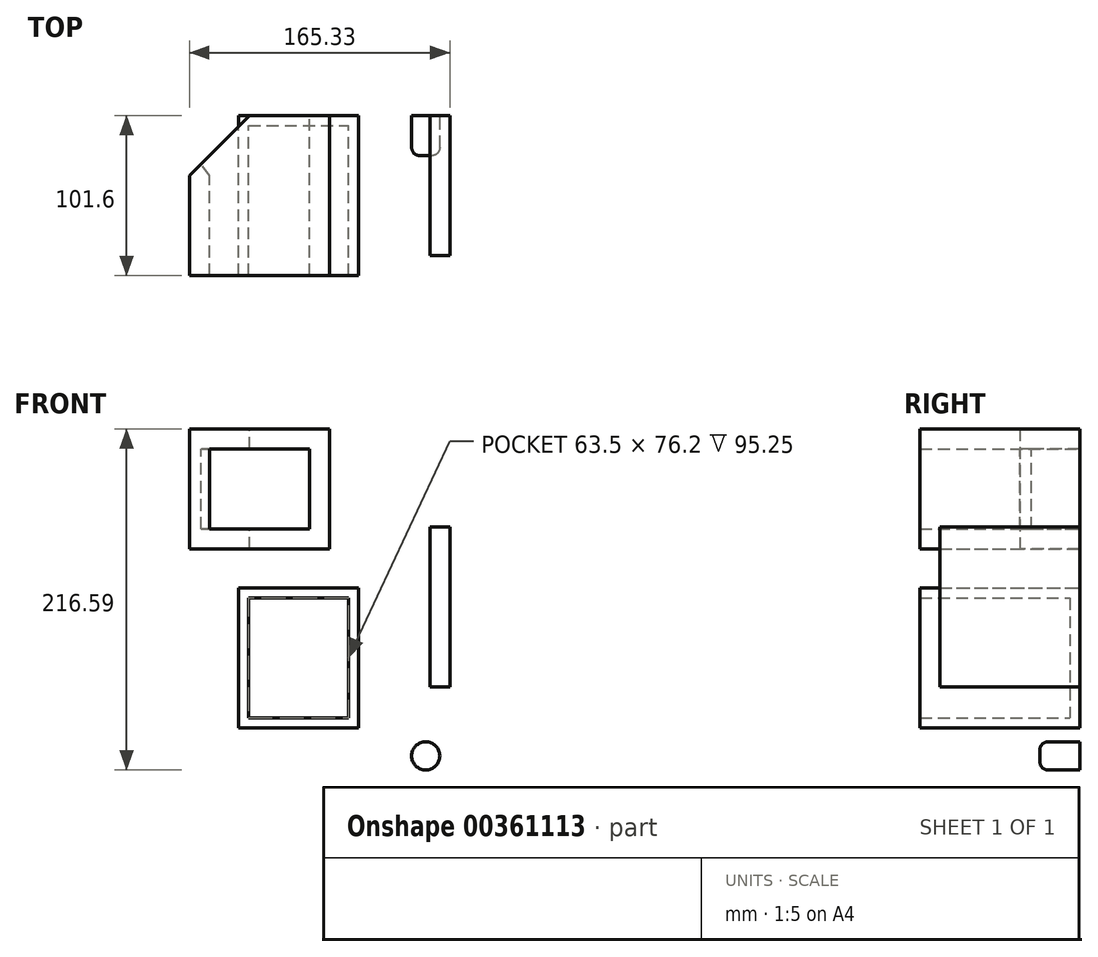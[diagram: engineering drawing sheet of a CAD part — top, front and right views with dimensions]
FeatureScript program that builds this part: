
annotation { "Feature Type Name" : "Feature", "Feature Type Description" : "" }
export const myFeature = defineFeature(function(context is Context, id is Id, definition is map)
    precondition{}
    {
        {
            var Q0;
            Q0=qCreatedBy(makeId("Front.planeOp"),FACE);
            var sketch = newSketch(context, id + "F0", { "sketchPlane" : qUnion([Q0])});
            skLineSegment(sketch, "E0.bottom", {"start": v(45.2, 26.89) * mm, "end": v(57.9, 26.89) * mm});
            skLineSegment(sketch, "E0.top", {"start": v(45.2, -74.71) * mm, "end": v(57.9, -74.71) * mm});
            skLineSegment(sketch, "E0.left", {"start": v(45.2, 26.89) * mm, "end": v(45.2, -74.71) * mm});
            skLineSegment(sketch, "E0.right", {"start": v(57.9, 26.89) * mm, "end": v(57.9, -74.71) * mm});
            skLineSegment(sketch, "E1.bottom", {"start": v(-31.24, 25.48) * mm, "end": v(-94.74, 25.48) * mm});
            skLineSegment(sketch, "E1.top", {"start": v(-31.24, 76.28) * mm, "end": v(-94.74, 76.28) * mm});
            skLineSegment(sketch, "E1.left", {"start": v(-31.24, 25.48) * mm, "end": v(-31.24, 76.28) * mm});
            skLineSegment(sketch, "E1.right", {"start": v(-94.74, 25.48) * mm, "end": v(-94.74, 76.28) * mm});
            skLineSegment(sketch, "E2.bottom", {"start": v(-107.44, 88.98) * mm, "end": v(-18.54, 88.98) * mm});
            skLineSegment(sketch, "E2.top", {"start": v(-107.44, 12.78) * mm, "end": v(-18.54, 12.78) * mm});
            skLineSegment(sketch, "E2.left", {"start": v(-107.44, 88.98) * mm, "end": v(-107.44, 12.78) * mm});
            skLineSegment(sketch, "E2.right", {"start": v(-18.54, 88.98) * mm, "end": v(-18.54, 12.78) * mm});
            skSolve(sketch);
        }
        {
            var Q0;
            Q0=makeQuery(id+"F0.imprint","IMPRINT",FACE,{"disambiguationData":[TD([[makeQuery(id+"F0.imprint","IMPRINT",EDGE,{"derivedFrom":sQuery(id+"F0.wireOp",EDGE,"E0.bottom")}),-1.0]])]});
            extrude(context, id + "F1", {"entities" : qUnion([Q0]), "depth" : 88.9 * mm});
        }
        {
            var Q0;
            Q0=makeQuery(id+"F0.imprint","IMPRINT",FACE,{"disambiguationData":[TD([[makeQuery(id+"F0.imprint","IMPRINT",EDGE,{"derivedFrom":sQuery(id+"F0.wireOp",EDGE,"E1.bottom")}),1.0]])]});
            extrude(context, id + "F2", {"entities" : qUnion([Q0]), "depth" : 101.6 * mm});
        }
        {
            var Q0;
            Q0=makeQuery(id+"F2.opExtrude","CAP_EDGE",EDGE,{"disambiguationData":[OSD([sQuery(id+"F0.wireOp",EDGE,"E2.left")])],"isStart":true});
            chamfer(context, id + "F3", {"entities" : qUnion([Q0]), "width" : 38.1 * mm, "tangentPropagation" : true});
        }
        {
            var Q0;
            Q0=makeQuery(id+"F3.opChamfer","BLEND_EDGE",EDGE,{"blendedFrom":[makeQuery(id+"F2.opExtrude","CAP_EDGE",EDGE,{"disambiguationData":[OSD([sQuery(id+"F0.wireOp",EDGE,"E2.left")])],"isStart":true}),makeQuery(id+"F2.opExtrude","SWEPT_FACE",FACE,{"disambiguationData":[OSD([sQuery(id+"F0.wireOp",EDGE,"E1.right")])]})],"blendedInto":[makeQuery(id+"F2.opExtrude","SWEPT_FACE",FACE,{"disambiguationData":[OSD([sQuery(id+"F0.wireOp",EDGE,"E1.right")])]})]});
            chamfer(context, id + "F4", {"entities" : qUnion([Q0]), "chamferType" : ChamferType.TWO_OFFSETS, "width1" : 12.7 * mm, "oppositeDirection" : false, "width2" : 7.62 * mm, "tangentPropagation" : true});
        }
        {
            var Q0;
            Q0=qCreatedBy(makeId("Front.planeOp"),FACE);
            var sketch = newSketch(context, id + "F5", { "sketchPlane" : qUnion([Q0])});
            skLineSegment(sketch, "E3.bottom", {"start": v(-76.2, -12.08) * mm, "end": v(0, -12.08) * mm});
            skLineSegment(sketch, "E3.top", {"start": v(-76.2, -100.98) * mm, "end": v(0, -100.98) * mm});
            skLineSegment(sketch, "E3.left", {"start": v(-76.2, -12.08) * mm, "end": v(-76.2, -100.98) * mm});
            skLineSegment(sketch, "E3.right", {"start": v(0, -12.08) * mm, "end": v(0, -100.98) * mm});
            skSolve(sketch);
        }
        {
            var Q0;
            Q0=makeQuery(id+"F5.imprint","IMPRINT",FACE,{"disambiguationData":[TD([[makeQuery(id+"F5.imprint","IMPRINT",EDGE,{"derivedFrom":sQuery(id+"F5.wireOp",EDGE,"E3.bottom")}),-1.0]])]});
            extrude(context, id + "F6", {"entities" : qUnion([Q0]), "depth" : 101.6 * mm});
        }
        {
            var Q0;
            Q0=makeQuery(id+"F6.opExtrude","CAP_FACE",FACE,{"disambiguationData":[OSD([sQuery(id+"F5.wireOp",EDGE,"E3.bottom"),sQuery(id+"F5.wireOp",EDGE,"E3.top"),sQuery(id+"F5.wireOp",EDGE,"E3.left"),sQuery(id+"F5.wireOp",EDGE,"E3.right")])],"isStart":false});
            shell(context, id + "F7", {"entities" : qUnion([Q0]), "thickness" : 6.35 * mm});
        }
        {
            var Q0;
            Q0=qCreatedBy(makeId("Front.planeOp"),FACE);
            var sketch = newSketch(context, id + "F8", { "sketchPlane" : qUnion([Q0])});
            skCircle(sketch, "E4", {"center": v(42.58, -118.65) * mm, "radius": 8.96 * mm});
            skSolve(sketch);
        }
        {
            var Q0;
            Q0=makeQuery(id+"F8.imprint","IMPRINT",FACE,{"disambiguationData":[TD([[makeQuery(id+"F8.imprint","IMPRINT",EDGE,{"derivedFrom":sQuery(id+"F8.wireOp",EDGE,"E4")}),1.0]])]});
            extrude(context, id + "F9", {"entities" : qUnion([Q0]), "depth" : 25.4 * mm});
        }
        {
            var Q0;
            Q0=makeQuery(id+"F9.opExtrude","CAP_EDGE",EDGE,{"disambiguationData":[OSD([sQuery(id+"F8.wireOp",EDGE,"E4")])],"isStart":false});
            fillet(context, id + "F10", {"entities" : qUnion([Q0]), "radius" : 5.08 * mm, "tangentPropagation" : true, "allowEdgeOverflow" : false});
        }
    });
